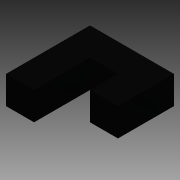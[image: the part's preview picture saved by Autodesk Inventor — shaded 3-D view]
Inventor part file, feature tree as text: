
AUTODESK INVENTOR PART (.ipt)
format: ipt  version: 2015 (Build 190159000, 159)  size: 81,408 bytes
history: native  units: in
note: dims shown in document units (in); Inventor stores cm internally (conversion verified against a paired STEP export)
features: extrude x1, sketch x1
ambient origin geometry x8: Origin, YZ Plane, XZ Plane, XY Plane, X Axis, Y Axis, Z Axis, Center Point
bodies: Solid1 (feature_tree)
feature tree (2):
  extrude  "Extrusion1"  Depth=2.25in
  sketch  "Sketch1"  dims[d0=2.25in d1=2.25in d2=1.5in d3=1.5in d4=0.75in d5=0.75in d6=0.75in d7=0.0in]
